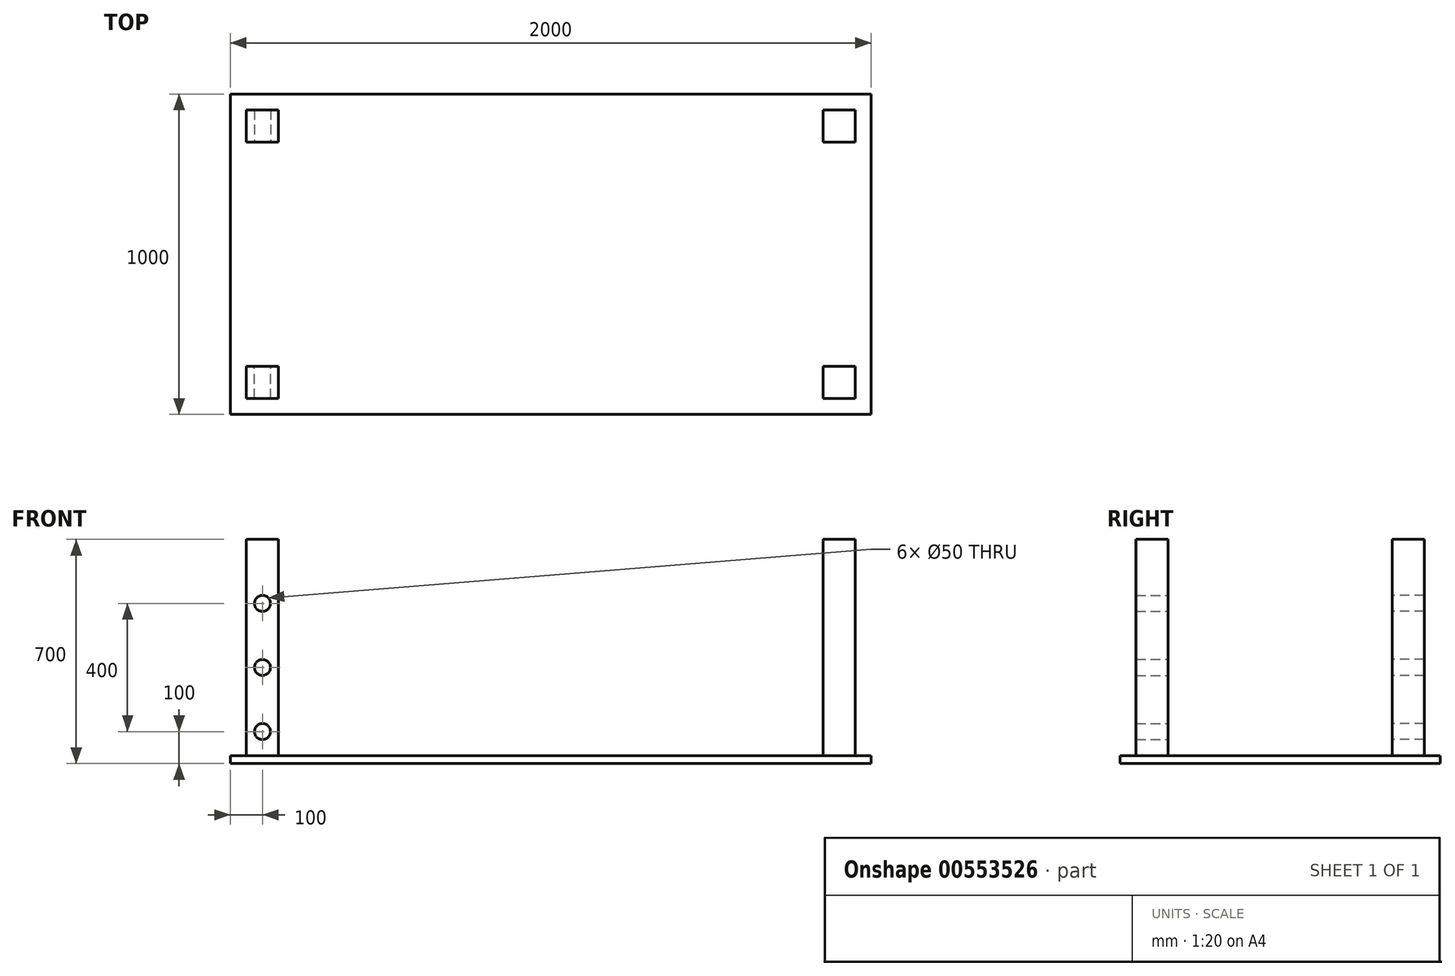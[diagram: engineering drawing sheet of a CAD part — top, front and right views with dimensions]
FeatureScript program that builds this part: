
annotation { "Feature Type Name" : "Feature", "Feature Type Description" : "" }
export const myFeature = defineFeature(function(context is Context, id is Id, definition is map)
    precondition{}
    {
        {
            var Q0;
            Q0=qCreatedBy(makeId("Top.planeOp"),FACE);
            var sketch = newSketch(context, id + "F0", { "sketchPlane" : qUnion([Q0])});
            skLineSegment(sketch, "E0.bottom", {"start": v(-1000, 500) * mm, "end": v(1000, 500) * mm});
            skLineSegment(sketch, "E0.top", {"start": v(-1000, -500) * mm, "end": v(1000, -500) * mm});
            skLineSegment(sketch, "E0.left", {"start": v(-1000, 500) * mm, "end": v(-1000, -500) * mm});
            skLineSegment(sketch, "E0.right", {"start": v(1000, 500) * mm, "end": v(1000, -500) * mm});
            skPoint(sketch, "E0.middle", {"position": v(0, 0) * mm});
            skSolve(sketch);
        }
        {
            var Q0;
            Q0 = qSketchRegion(id + "F0", true);
            extrude(context, id + "F1", {"entities" : qUnion([Q0]), "depth" : 25 * mm, "offsetDistance" : 25 * mm});
        }
        {
            var Q0;
            Q0=qCreatedBy(makeId("Top.planeOp"),FACE);
            var sketch = newSketch(context, id + "F2", { "sketchPlane" : qUnion([Q0])});
            skLineSegment(sketch, "E1.bottom", {"start": v(-850, 350) * mm, "end": v(-950, 350) * mm});
            skLineSegment(sketch, "E1.top", {"start": v(-850, 450) * mm, "end": v(-950, 450) * mm});
            skLineSegment(sketch, "E1.left", {"start": v(-850, 350) * mm, "end": v(-850, 450) * mm});
            skLineSegment(sketch, "E1.right", {"start": v(-950, 350) * mm, "end": v(-950, 450) * mm});
            skPoint(sketch, "E1.middle", {"position": v(-900, 400) * mm});
            skLineSegment(sketch, "E2.bottom", {"start": v(-850, -450) * mm, "end": v(-950, -450) * mm});
            skLineSegment(sketch, "E2.top", {"start": v(-850, -350) * mm, "end": v(-950, -350) * mm});
            skLineSegment(sketch, "E2.left", {"start": v(-850, -450) * mm, "end": v(-850, -350) * mm});
            skLineSegment(sketch, "E2.right", {"start": v(-950, -450) * mm, "end": v(-950, -350) * mm});
            skPoint(sketch, "E2.middle", {"position": v(-900, -400) * mm});
            skLineSegment(sketch, "E3.bottom", {"start": v(950, 350) * mm, "end": v(850, 350) * mm});
            skLineSegment(sketch, "E3.top", {"start": v(950, 450) * mm, "end": v(850, 450) * mm});
            skLineSegment(sketch, "E3.left", {"start": v(950, 350) * mm, "end": v(950, 450) * mm});
            skLineSegment(sketch, "E3.right", {"start": v(850, 350) * mm, "end": v(850, 450) * mm});
            skPoint(sketch, "E3.middle", {"position": v(900, 400) * mm});
            skLineSegment(sketch, "E4.bottom", {"start": v(950, -450) * mm, "end": v(850, -450) * mm});
            skLineSegment(sketch, "E4.top", {"start": v(950, -350) * mm, "end": v(850, -350) * mm});
            skLineSegment(sketch, "E4.left", {"start": v(950, -450) * mm, "end": v(950, -350) * mm});
            skLineSegment(sketch, "E4.right", {"start": v(850, -450) * mm, "end": v(850, -350) * mm});
            skPoint(sketch, "E4.middle", {"position": v(900, -400) * mm});
            skSolve(sketch);
        }
        {
            var Q0;
            Q0 = qSketchRegion(id + "F2", true);
            extrude(context, id + "F3", {"entities" : qUnion([Q0]), "operationType" : NewBodyOperationType.ADD, "depth" : 700 * mm, "offsetDistance" : 25 * mm});
        }
        {
            var Q0;
            Q0=qCreatedBy(makeId("Front.planeOp"),FACE);
            var sketch = newSketch(context, id + "F4", { "sketchPlane" : qUnion([Q0])});
            skCircle(sketch, "E5", {"center": v(-900, 100) * mm, "radius": 24.45 * mm});
            skCircle(sketch, "E6", {"center": v(-900, 300) * mm, "radius": 24.51 * mm});
            skCircle(sketch, "E7", {"center": v(-900, 500) * mm, "radius": 24.45 * mm});
            skSolve(sketch);
        }
        {
            var Q0;
            Q0=sQuery(id+"F4.wireOp",VERTEX,"E7.center");
            var Q1;
            Q1=sQuery(id+"F4.wireOp",VERTEX,"E6.center");
            var Q2;
            Q2=sQuery(id+"F4.wireOp",VERTEX,"E5.center");
            var Q3;
            Q3=makeQuery(id+"F1.opExtrude","SWEPT_BODY",BODY,{"disambiguationData":[OSD([sQuery(id+"F0.wireOp",EDGE,"E0.bottom"),sQuery(id+"F0.wireOp",EDGE,"E0.top"),sQuery(id+"F0.wireOp",EDGE,"E0.left"),sQuery(id+"F0.wireOp",EDGE,"E0.right")])]});
            hole(context, id + "F5", {"style" : HoleStyle.SIMPLE, "endStyle" : HoleEndStyle.THROUGH, "oppositeDirection" : true, "holeDiameter" : 50 * mm, "isTappedThrough" : true, "tappedDepth" : 12 * mm, "tapClearance" : 3, "locations" : qUnion([Q0, Q1, Q2]), "scope" : qUnion([Q3])});
        }
        {
            var Q0;
            Q0=sQuery(id+"F4.wireOp",VERTEX,"E6.center");
            var Q1;
            Q1=sQuery(id+"F4.wireOp",VERTEX,"E7.center");
            var Q2;
            Q2=sQuery(id+"F4.wireOp",VERTEX,"E5.center");
            var Q3;
            Q3=makeQuery(id+"F1.opExtrude","SWEPT_BODY",BODY,{"disambiguationData":[OSD([sQuery(id+"F0.wireOp",EDGE,"E0.bottom"),sQuery(id+"F0.wireOp",EDGE,"E0.top"),sQuery(id+"F0.wireOp",EDGE,"E0.left"),sQuery(id+"F0.wireOp",EDGE,"E0.right")])]});
            hole(context, id + "F6", {"style" : HoleStyle.SIMPLE, "endStyle" : HoleEndStyle.THROUGH, "holeDiameter" : 50 * mm, "isTappedThrough" : true, "tappedDepth" : 12 * mm, "tapClearance" : 3, "locations" : qUnion([Q0, Q1, Q2]), "scope" : qUnion([Q3])});
        }
    });
